# Revit family: FU_Chair_Sandler_Loft Soft 085-13
name_source: partatom
category: Furniture
units: mm (PartAtom-declared; Revit-internal decimal feet)

## family parameters
Always vertical = Yes
Cut with Voids When Loaded = No
OmniClass Number = 23.40.20.00
OmniClass Title = General Furniture and Specialties
Room Calculation Point = No
Shared = No
Work Plane-Based = No

## types (1)
- Loft 085.13
    Default Elevation = 0 mm  [stored 0 ft]
    Depth = 920 mm  [stored 3.01837 ft]
    Description = Lounge chair with extra cushioned upholstery on swivel base in polished chrome or matt black finish. Additional foot stool available. 360 Swivel with memory return.
    Height = 1100 mm
    Manufacturer = Sandler
    Model = Loft 085.13
    Shell = Leather - Black - Sandler 101
    URL = https://www.sandlerseating.com
    Width = 830 mm  [stored 2.7231 ft]

note: [stored X ft] marks values corroborated as IEEE doubles in the binary element streams (Revit-internal decimal feet)

## geometry (parser evidence)
native form markers: Sweep x2
no freeform markers — native parametric forms only
